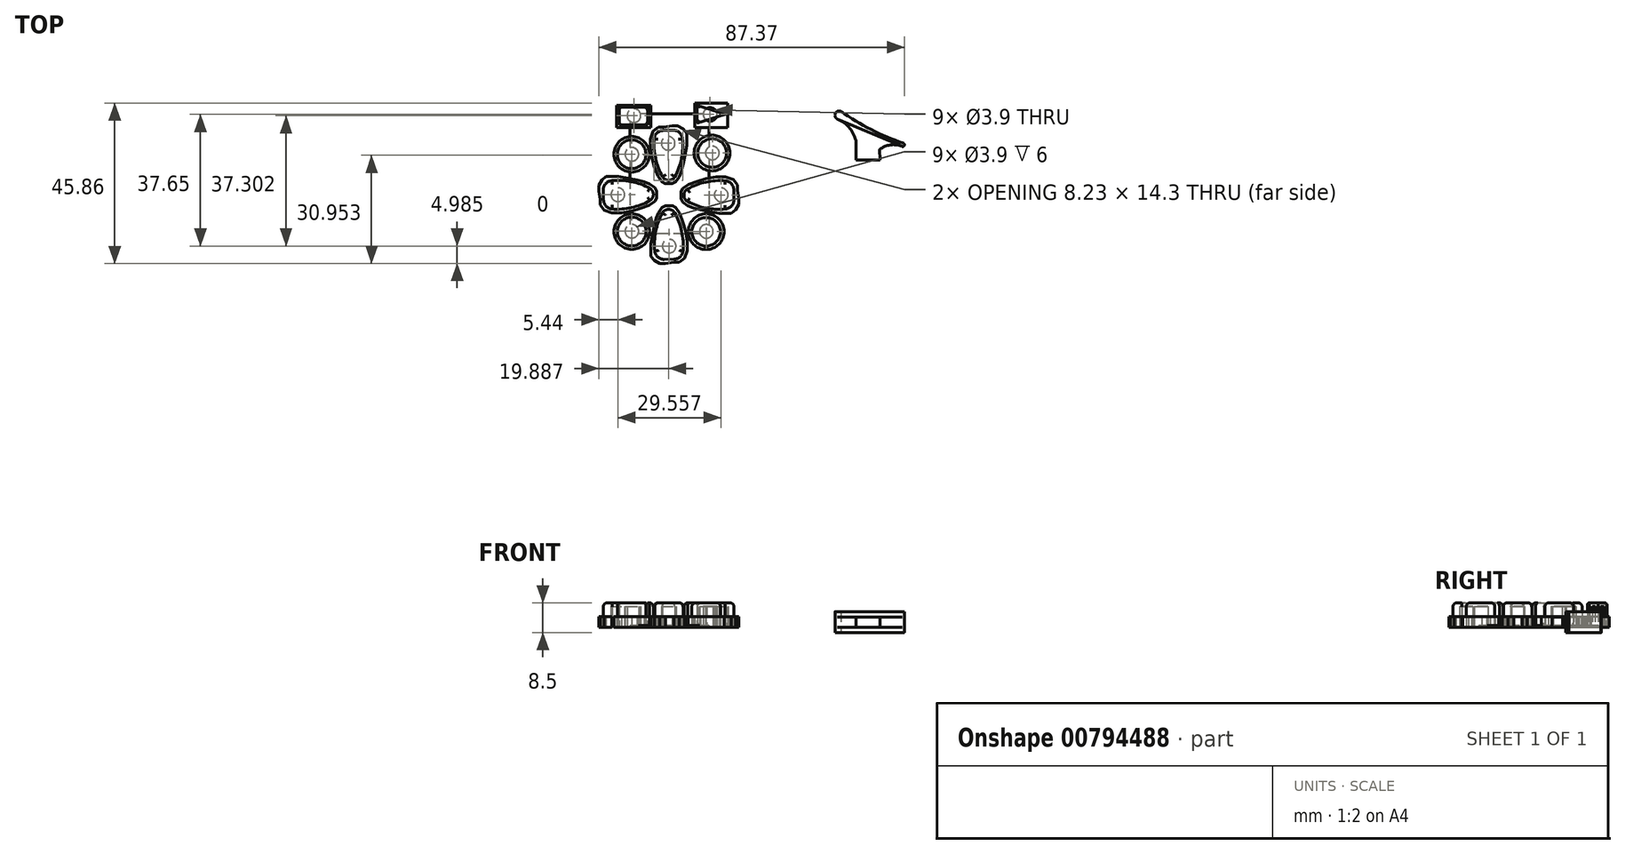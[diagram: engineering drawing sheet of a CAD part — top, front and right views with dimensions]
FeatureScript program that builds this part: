
annotation { "Feature Type Name" : "Feature", "Feature Type Description" : "" }
export const myFeature = defineFeature(function(context is Context, id is Id, definition is map)
    precondition{}
    {
        {
            var Q0;
            Q0=qCreatedBy(makeId("Top.planeOp"),FACE);
            var sketch = newSketch(context, id + "F0", { "sketchPlane" : qUnion([Q0])});
            skCircle(sketch, "E0", {"center": v(-35, -19.65) * mm, "radius": 4.1 * mm});
            skCircle(sketch, "E1", {"center": v(-58, -42.1) * mm, "radius": 4.1 * mm});
            skCircle(sketch, "E2", {"center": v(-58.02, -20.01) * mm, "radius": 4.1 * mm});
            skCircle(sketch, "E3", {"center": v(-36.71, -42.18) * mm, "radius": 4.1 * mm});
            skLineSegment(sketch, "E4", {"start": v(-39.3, -6.04) * mm, "end": v(-39.3, -11.07) * mm});
            skLineSegment(sketch, "E5", {"start": v(-39.3, -11.07) * mm, "end": v(-31.18, -8.6) * mm});
            skLineSegment(sketch, "E6", {"start": v(-31.18, -8.6) * mm, "end": v(-39.3, -6.04) * mm});
            skLineSegment(sketch, "E7", {"start": v(-61.5, -6.54) * mm, "end": v(-61.5, -11.57) * mm});
            skLineSegment(sketch, "E8", {"start": v(-61.5, -11.57) * mm, "end": v(-53.42, -11.57) * mm});
            skLineSegment(sketch, "E9", {"start": v(-53.42, -11.57) * mm, "end": v(-53.42, -6.54) * mm});
            skLineSegment(sketch, "E10", {"start": v(-53.42, -6.54) * mm, "end": v(-61.5, -6.54) * mm});
            skArc(sketch, "E11", {"start": v(-48.98, -13.2) * mm, "mid": v(-50.76, -13.92) * mm, "end": v(-51.58, -15.64) * mm});
            skLineSegment(sketch, "E12", {"start": v(-48.98, -13.2) * mm, "end": v(-46.14, -13.15) * mm});
            skArc(sketch, "E13", {"start": v(-43.48, -15.64) * mm, "mid": v(-44.3, -13.85) * mm, "end": v(-46.14, -13.15) * mm});
            skArc(sketch, "E14", {"start": v(-45.62, -26.42) * mm, "mid": v(-43.76, -21.19) * mm, "end": v(-43.48, -15.64) * mm});
            skArc(sketch, "E15", {"start": v(-51.58, -15.64) * mm, "mid": v(-51.17, -21.2) * mm, "end": v(-49.2, -26.42) * mm});
            skArc(sketch, "E16", {"start": v(-49.2, -26.42) * mm, "mid": v(-47.41, -27.45) * mm, "end": v(-45.62, -26.42) * mm});
            skArc(sketch, "E17", {"start": v(-66.07, -33.05) * mm, "mid": v(-65.35, -34.82) * mm, "end": v(-63.63, -35.65) * mm});
            skLineSegment(sketch, "E18", {"start": v(-66.07, -33.05) * mm, "end": v(-66.12, -30.2) * mm});
            skArc(sketch, "E19", {"start": v(-63.63, -27.55) * mm, "mid": v(-65.41, -28.37) * mm, "end": v(-66.12, -30.2) * mm});
            skArc(sketch, "E20", {"start": v(-52.85, -29.69) * mm, "mid": v(-58.08, -27.82) * mm, "end": v(-63.63, -27.55) * mm});
            skArc(sketch, "E21", {"start": v(-63.63, -35.65) * mm, "mid": v(-58.07, -35.24) * mm, "end": v(-52.85, -33.28) * mm});
            skArc(sketch, "E22", {"start": v(-52.85, -33.28) * mm, "mid": v(-51.82, -31.48) * mm, "end": v(-52.85, -29.69) * mm});
            skArc(sketch, "E23", {"start": v(-45.9, -50) * mm, "mid": v(-44.13, -49.29) * mm, "end": v(-43.3, -47.56) * mm});
            skLineSegment(sketch, "E24", {"start": v(-45.9, -50) * mm, "end": v(-48.75, -50.06) * mm});
            skArc(sketch, "E25", {"start": v(-51.4, -47.56) * mm, "mid": v(-50.58, -49.35) * mm, "end": v(-48.75, -50.06) * mm});
            skArc(sketch, "E26", {"start": v(-49.27, -36.78) * mm, "mid": v(-51.13, -42.02) * mm, "end": v(-51.4, -47.56) * mm});
            skArc(sketch, "E27", {"start": v(-43.3, -47.56) * mm, "mid": v(-43.71, -42) * mm, "end": v(-45.68, -36.78) * mm});
            skArc(sketch, "E28", {"start": v(-45.68, -36.78) * mm, "mid": v(-47.47, -35.76) * mm, "end": v(-49.27, -36.78) * mm});
            skArc(sketch, "E29", {"start": v(-28.82, -30.15) * mm, "mid": v(-29.54, -28.38) * mm, "end": v(-31.26, -27.55) * mm});
            skLineSegment(sketch, "E30", {"start": v(-28.82, -30.15) * mm, "end": v(-28.77, -33) * mm});
            skArc(sketch, "E31", {"start": v(-31.26, -35.66) * mm, "mid": v(-29.47, -34.83) * mm, "end": v(-28.77, -33) * mm});
            skArc(sketch, "E32", {"start": v(-42.04, -33.51) * mm, "mid": v(-36.8, -35.38) * mm, "end": v(-31.26, -35.66) * mm});
            skArc(sketch, "E33", {"start": v(-31.26, -27.55) * mm, "mid": v(-36.82, -27.96) * mm, "end": v(-42.04, -29.93) * mm});
            skArc(sketch, "E34", {"start": v(-42.04, -29.93) * mm, "mid": v(-43.07, -31.72) * mm, "end": v(-42.04, -33.51) * mm});
            skSolve(sketch);
        }
        {
            var Q0;
            Q0=makeQuery(id+"F0.imprint","IMPRINT",FACE,{"disambiguationData":[TD([[makeQuery(id+"F0.imprint","IMPRINT",EDGE,{"derivedFrom":sQuery(id+"F0.wireOp",EDGE,"E0")}),1.0]])]});
            var Q1;
            Q1=makeQuery(id+"F0.imprint","IMPRINT",FACE,{"disambiguationData":[TD([[makeQuery(id+"F0.imprint","IMPRINT",EDGE,{"derivedFrom":sQuery(id+"F0.wireOp",EDGE,"E1")}),1.0]])]});
            var Q2;
            Q2=makeQuery(id+"F0.imprint","IMPRINT",FACE,{"disambiguationData":[TD([[makeQuery(id+"F0.imprint","IMPRINT",EDGE,{"derivedFrom":sQuery(id+"F0.wireOp",EDGE,"E2")}),1.0]])]});
            var Q3;
            Q3=makeQuery(id+"F0.imprint","IMPRINT",FACE,{"disambiguationData":[TD([[makeQuery(id+"F0.imprint","IMPRINT",EDGE,{"derivedFrom":sQuery(id+"F0.wireOp",EDGE,"E3")}),1.0]])]});
            var Q4;
            Q4=makeQuery(id+"F0.imprint","IMPRINT",FACE,{"disambiguationData":[TD([[makeQuery(id+"F0.imprint","IMPRINT",EDGE,{"derivedFrom":sQuery(id+"F0.wireOp",EDGE,"E4")}),1.0]])]});
            var Q5;
            Q5=makeQuery(id+"F0.imprint","IMPRINT",FACE,{"disambiguationData":[TD([[makeQuery(id+"F0.imprint","IMPRINT",EDGE,{"derivedFrom":sQuery(id+"F0.wireOp",EDGE,"E7")}),1.0]])]});
            var Q6;
            Q6=makeQuery(id+"F0.imprint","IMPRINT",FACE,{"disambiguationData":[TD([[makeQuery(id+"F0.imprint","IMPRINT",EDGE,{"derivedFrom":sQuery(id+"F0.wireOp",EDGE,"E11")}),1.0]])]});
            var Q7;
            Q7=makeQuery(id+"F0.imprint","IMPRINT",FACE,{"disambiguationData":[TD([[makeQuery(id+"F0.imprint","IMPRINT",EDGE,{"derivedFrom":sQuery(id+"F0.wireOp",EDGE,"E17")}),1.0]])]});
            var Q8;
            Q8=makeQuery(id+"F0.imprint","IMPRINT",FACE,{"disambiguationData":[TD([[makeQuery(id+"F0.imprint","IMPRINT",EDGE,{"derivedFrom":sQuery(id+"F0.wireOp",EDGE,"E23")}),1.0]])]});
            var Q9;
            Q9=makeQuery(id+"F0.imprint","IMPRINT",FACE,{"disambiguationData":[TD([[makeQuery(id+"F0.imprint","IMPRINT",EDGE,{"derivedFrom":sQuery(id+"F0.wireOp",EDGE,"E29")}),1.0]])]});
            extrude(context, id + "F1", {"entities" : qUnion([Q0, Q1, Q2, Q3, Q4, Q5, Q6, Q7, Q8, Q9]), "depth" : 7 * mm, "offsetDistance" : 25 * mm});
        }
        {
            var Q0;
            Q0=makeQuery(id+"F1.opExtrude","CAP_FACE",FACE,{"disambiguationData":[OSD([sQuery(id+"F0.wireOp",EDGE,"E11"),sQuery(id+"F0.wireOp",EDGE,"E12"),sQuery(id+"F0.wireOp",EDGE,"E13"),sQuery(id+"F0.wireOp",EDGE,"E14"),sQuery(id+"F0.wireOp",EDGE,"E15"),sQuery(id+"F0.wireOp",EDGE,"E16")])],"isStart":false});
            var Q1;
            Q1=makeQuery(id+"F1.opExtrude","CAP_FACE",FACE,{"disambiguationData":[OSD([sQuery(id+"F0.wireOp",EDGE,"E2")])],"isStart":false});
            var Q2;
            Q2=makeQuery(id+"F1.opExtrude","CAP_FACE",FACE,{"disambiguationData":[OSD([sQuery(id+"F0.wireOp",EDGE,"E17"),sQuery(id+"F0.wireOp",EDGE,"E18"),sQuery(id+"F0.wireOp",EDGE,"E19"),sQuery(id+"F0.wireOp",EDGE,"E20"),sQuery(id+"F0.wireOp",EDGE,"E21"),sQuery(id+"F0.wireOp",EDGE,"E22")])],"isStart":false});
            var Q3;
            Q3=makeQuery(id+"F1.opExtrude","CAP_FACE",FACE,{"disambiguationData":[OSD([sQuery(id+"F0.wireOp",EDGE,"E0")])],"isStart":false});
            var Q4;
            Q4=makeQuery(id+"F1.opExtrude","CAP_FACE",FACE,{"disambiguationData":[OSD([sQuery(id+"F0.wireOp",EDGE,"E29"),sQuery(id+"F0.wireOp",EDGE,"E30"),sQuery(id+"F0.wireOp",EDGE,"E31"),sQuery(id+"F0.wireOp",EDGE,"E32"),sQuery(id+"F0.wireOp",EDGE,"E33"),sQuery(id+"F0.wireOp",EDGE,"E34")])],"isStart":false});
            var Q5;
            Q5=makeQuery(id+"F1.opExtrude","CAP_FACE",FACE,{"disambiguationData":[OSD([sQuery(id+"F0.wireOp",EDGE,"E3")])],"isStart":false});
            var Q6;
            Q6=makeQuery(id+"F1.opExtrude","CAP_FACE",FACE,{"disambiguationData":[OSD([sQuery(id+"F0.wireOp",EDGE,"E23"),sQuery(id+"F0.wireOp",EDGE,"E24"),sQuery(id+"F0.wireOp",EDGE,"E25"),sQuery(id+"F0.wireOp",EDGE,"E26"),sQuery(id+"F0.wireOp",EDGE,"E27"),sQuery(id+"F0.wireOp",EDGE,"E28")])],"isStart":false});
            fillet(context, id + "F2", {"entities" : qUnion([Q0, Q1, Q2, Q3, Q4, Q5, Q6]), "radius" : 1.12 * mm, "tangentPropagation" : true, "allowEdgeOverflow" : false});
        }
        {
            var Q0;
            Q0=makeQuery(id+"F1.opExtrude","CAP_FACE",FACE,{"disambiguationData":[OSD([sQuery(id+"F0.wireOp",EDGE,"E7"),sQuery(id+"F0.wireOp",EDGE,"E8"),sQuery(id+"F0.wireOp",EDGE,"E9"),sQuery(id+"F0.wireOp",EDGE,"E10")])],"isStart":false});
            var Q1;
            Q1=makeQuery(id+"F1.opExtrude","CAP_FACE",FACE,{"disambiguationData":[OSD([sQuery(id+"F0.wireOp",EDGE,"E4"),sQuery(id+"F0.wireOp",EDGE,"E5"),sQuery(id+"F0.wireOp",EDGE,"E6")])],"isStart":false});
            fillet(context, id + "F3", {"entities" : qUnion([Q0, Q1]), "radius" : .5 * mm, "tangentPropagation" : true, "allowEdgeOverflow" : false});
        }
        {
            var Q0;
            Q0=makeQuery(id+"F1.opExtrude","CAP_FACE",FACE,{"disambiguationData":[OSD([sQuery(id+"F0.wireOp",EDGE,"E11"),sQuery(id+"F0.wireOp",EDGE,"E12"),sQuery(id+"F0.wireOp",EDGE,"E13"),sQuery(id+"F0.wireOp",EDGE,"E14"),sQuery(id+"F0.wireOp",EDGE,"E15"),sQuery(id+"F0.wireOp",EDGE,"E16")])],"isStart":true});
            var sketch = newSketch(context, id + "F4", { "sketchPlane" : qUnion([Q0])});
            skCircle(sketch, "E35", {"center": v(-57.95, 20.02) * mm, "radius": 1.95 * mm});
            skCircle(sketch, "E36", {"center": v(-34.94, 19.66) * mm, "radius": 1.95 * mm});
            skCircle(sketch, "E37", {"center": v(-36.66, 42.04) * mm, "radius": 1.95 * mm});
            skCircle(sketch, "E38", {"center": v(-57.95, 42.01) * mm, "radius": 1.95 * mm});
            skCircle(sketch, "E39", {"center": v(-32.4, 31.62) * mm, "radius": 1.95 * mm});
            skCircle(sketch, "E40", {"center": v(-61.96, 31.55) * mm, "radius": 1.95 * mm});
            skCircle(sketch, "E41", {"center": v(-47.28, 46.26) * mm, "radius": 1.95 * mm});
            skCircle(sketch, "E42", {"center": v(-47.56, 16.87) * mm, "radius": 1.95 * mm});
            skPoint(sketch, "E43", {"position": v(-47.56, 13.17) * mm});
            skCircle(sketch, "E44", {"center": v(-57.36, 8.96) * mm, "radius": 1.95 * mm});
            skCircle(sketch, "E45", {"center": v(-35.59, 8.61) * mm, "radius": 1.95 * mm});
            skSolve(sketch);
        }
        {
            var Q0;
            Q0=makeQuery(id+"F4.imprint","IMPRINT",FACE,{"disambiguationData":[TD([[makeQuery(id+"F4.imprint","IMPRINT",EDGE,{"derivedFrom":sQuery(id+"F4.wireOp",EDGE,"E42")}),-1.0]])]});
            var sketch = newSketch(context, id + "F5", { "sketchPlane" : qUnion([Q0])});
            skCircle(sketch, "E46", {"center": v(-35.06, 19.67) * mm, "radius": 5.1 * mm});
            skCircle(sketch, "E47", {"center": v(-58, 20) * mm, "radius": 5.1 * mm});
            skCircle(sketch, "E48", {"center": v(-57.97, 42.11) * mm, "radius": 5.1 * mm});
            skCircle(sketch, "E49", {"center": v(-36.7, 42.13) * mm, "radius": 5.1 * mm});
            skLineSegment(sketch, "E50", {"start": v(-27.77, 30.26) * mm, "end": v(-27.77, 28.82) * mm});
            skLineSegment(sketch, "E51", {"start": v(-27.77, 28.82) * mm, "end": v(-28.94, 27.23) * mm});
            skLineSegment(sketch, "E52", {"start": v(-28.94, 27.23) * mm, "end": v(-31.14, 26.48) * mm});
            skLineSegment(sketch, "E53", {"start": v(-31.14, 26.48) * mm, "end": v(-33.85, 26.48) * mm});
            skLineSegment(sketch, "E54", {"start": v(-33.85, 26.48) * mm, "end": v(-36.84, 27) * mm});
            skLineSegment(sketch, "E55", {"start": v(-36.84, 27) * mm, "end": v(-39.18, 27.7) * mm});
            skLineSegment(sketch, "E56", {"start": v(-39.18, 27.7) * mm, "end": v(-41.75, 28.67) * mm});
            skLineSegment(sketch, "E57", {"start": v(-41.75, 28.67) * mm, "end": v(-43.4, 29.8) * mm});
            skLineSegment(sketch, "E58", {"start": v(-43.4, 29.8) * mm, "end": v(-43.95, 30.69) * mm});
            skLineSegment(sketch, "E59", {"start": v(-43.95, 30.69) * mm, "end": v(-43.95, 31.71) * mm});
            skLineSegment(sketch, "E60", {"start": v(-43.95, 31.71) * mm, "end": v(-43.95, 32.7) * mm});
            skLineSegment(sketch, "E61", {"start": v(-43.95, 32.7) * mm, "end": v(-43.4, 33.68) * mm});
            skLineSegment(sketch, "E62", {"start": v(-43.4, 33.68) * mm, "end": v(-41.94, 34.7) * mm});
            skLineSegment(sketch, "E63", {"start": v(-41.94, 34.7) * mm, "end": v(-40.35, 35.36) * mm});
            skLineSegment(sketch, "E64", {"start": v(-40.35, 35.36) * mm, "end": v(-38.3, 35.92) * mm});
            skLineSegment(sketch, "E65", {"start": v(-38.3, 35.92) * mm, "end": v(-35.72, 36.4) * mm});
            skLineSegment(sketch, "E66", {"start": v(-35.72, 36.4) * mm, "end": v(-33, 36.86) * mm});
            skLineSegment(sketch, "E67", {"start": v(-33, 36.86) * mm, "end": v(-31.1, 36.86) * mm});
            skLineSegment(sketch, "E68", {"start": v(-31.1, 36.86) * mm, "end": v(-29.5, 36.86) * mm});
            skLineSegment(sketch, "E69", {"start": v(-29.5, 36.86) * mm, "end": v(-28.24, 35.92) * mm});
            skLineSegment(sketch, "E70", {"start": v(-28.24, 35.92) * mm, "end": v(-27.4, 34.29) * mm});
            skLineSegment(sketch, "E71", {"start": v(-27.4, 34.29) * mm, "end": v(-27.4, 32.7) * mm});
            skLineSegment(sketch, "E72", {"start": v(-27.4, 32.7) * mm, "end": v(-27.77, 30.26) * mm});
            skLineSegment(sketch, "E73", {"start": v(-67.03, 32.97) * mm, "end": v(-67.03, 34.42) * mm});
            skLineSegment(sketch, "E74", {"start": v(-67.03, 34.42) * mm, "end": v(-65.86, 36) * mm});
            skLineSegment(sketch, "E75", {"start": v(-65.86, 36) * mm, "end": v(-63.66, 36.76) * mm});
            skLineSegment(sketch, "E76", {"start": v(-63.66, 36.76) * mm, "end": v(-60.95, 36.76) * mm});
            skLineSegment(sketch, "E77", {"start": v(-60.95, 36.76) * mm, "end": v(-57.96, 36.24) * mm});
            skLineSegment(sketch, "E78", {"start": v(-57.96, 36.24) * mm, "end": v(-55.62, 35.54) * mm});
            skLineSegment(sketch, "E79", {"start": v(-55.62, 35.54) * mm, "end": v(-53.05, 34.56) * mm});
            skLineSegment(sketch, "E80", {"start": v(-53.05, 34.56) * mm, "end": v(-51.41, 33.44) * mm});
            skLineSegment(sketch, "E81", {"start": v(-51.41, 33.44) * mm, "end": v(-50.85, 32.55) * mm});
            skLineSegment(sketch, "E82", {"start": v(-50.85, 32.55) * mm, "end": v(-50.85, 31.52) * mm});
            skLineSegment(sketch, "E83", {"start": v(-50.85, 31.52) * mm, "end": v(-50.85, 30.54) * mm});
            skLineSegment(sketch, "E84", {"start": v(-50.85, 30.54) * mm, "end": v(-51.41, 29.56) * mm});
            skLineSegment(sketch, "E85", {"start": v(-51.41, 29.56) * mm, "end": v(-52.86, 28.53) * mm});
            skLineSegment(sketch, "E86", {"start": v(-52.86, 28.53) * mm, "end": v(-54.45, 27.87) * mm});
            skLineSegment(sketch, "E87", {"start": v(-54.45, 27.87) * mm, "end": v(-56.5, 27.31) * mm});
            skLineSegment(sketch, "E88", {"start": v(-56.5, 27.31) * mm, "end": v(-59.08, 26.84) * mm});
            skLineSegment(sketch, "E89", {"start": v(-59.08, 26.84) * mm, "end": v(-61.8, 26.38) * mm});
            skLineSegment(sketch, "E90", {"start": v(-61.8, 26.38) * mm, "end": v(-63.7, 26.38) * mm});
            skLineSegment(sketch, "E91", {"start": v(-63.7, 26.38) * mm, "end": v(-65.3, 26.38) * mm});
            skLineSegment(sketch, "E92", {"start": v(-65.3, 26.38) * mm, "end": v(-66.56, 27.31) * mm});
            skLineSegment(sketch, "E93", {"start": v(-66.56, 27.31) * mm, "end": v(-67.4, 28.95) * mm});
            skLineSegment(sketch, "E94", {"start": v(-67.4, 28.95) * mm, "end": v(-67.4, 30.54) * mm});
            skLineSegment(sketch, "E95", {"start": v(-67.4, 30.54) * mm, "end": v(-67.03, 32.97) * mm});
            skLineSegment(sketch, "E96", {"start": v(-45.9, 50.88) * mm, "end": v(-44.46, 50.88) * mm});
            skLineSegment(sketch, "E97", {"start": v(-44.46, 50.88) * mm, "end": v(-42.87, 49.7) * mm});
            skLineSegment(sketch, "E98", {"start": v(-42.87, 49.7) * mm, "end": v(-42.12, 47.5) * mm});
            skLineSegment(sketch, "E99", {"start": v(-42.12, 47.5) * mm, "end": v(-42.12, 44.8) * mm});
            skLineSegment(sketch, "E100", {"start": v(-42.12, 44.8) * mm, "end": v(-42.63, 41.8) * mm});
            skLineSegment(sketch, "E101", {"start": v(-42.63, 41.8) * mm, "end": v(-43.33, 39.47) * mm});
            skLineSegment(sketch, "E102", {"start": v(-43.33, 39.47) * mm, "end": v(-44.32, 36.9) * mm});
            skLineSegment(sketch, "E103", {"start": v(-44.32, 36.9) * mm, "end": v(-45.44, 35.26) * mm});
            skLineSegment(sketch, "E104", {"start": v(-45.44, 35.26) * mm, "end": v(-46.33, 34.7) * mm});
            skLineSegment(sketch, "E105", {"start": v(-46.33, 34.7) * mm, "end": v(-47.36, 34.7) * mm});
            skLineSegment(sketch, "E106", {"start": v(-47.36, 34.7) * mm, "end": v(-48.34, 34.7) * mm});
            skLineSegment(sketch, "E107", {"start": v(-48.34, 34.7) * mm, "end": v(-49.32, 35.26) * mm});
            skLineSegment(sketch, "E108", {"start": v(-49.32, 35.26) * mm, "end": v(-50.35, 36.7) * mm});
            skLineSegment(sketch, "E109", {"start": v(-50.35, 36.7) * mm, "end": v(-51, 38.3) * mm});
            skLineSegment(sketch, "E110", {"start": v(-51, 38.3) * mm, "end": v(-51.56, 40.35) * mm});
            skLineSegment(sketch, "E111", {"start": v(-51.56, 40.35) * mm, "end": v(-52.03, 42.93) * mm});
            skLineSegment(sketch, "E112", {"start": v(-52.03, 42.93) * mm, "end": v(-52.5, 45.64) * mm});
            skLineSegment(sketch, "E113", {"start": v(-52.5, 45.64) * mm, "end": v(-52.5, 47.56) * mm});
            skLineSegment(sketch, "E114", {"start": v(-52.5, 47.56) * mm, "end": v(-52.5, 49.15) * mm});
            skLineSegment(sketch, "E115", {"start": v(-52.5, 49.15) * mm, "end": v(-51.56, 50.4) * mm});
            skLineSegment(sketch, "E116", {"start": v(-51.56, 50.4) * mm, "end": v(-49.93, 51.25) * mm});
            skLineSegment(sketch, "E117", {"start": v(-49.93, 51.25) * mm, "end": v(-48.34, 51.25) * mm});
            skLineSegment(sketch, "E118", {"start": v(-48.34, 51.25) * mm, "end": v(-45.9, 50.88) * mm});
            skLineSegment(sketch, "E119", {"start": v(-48.89, 12.25) * mm, "end": v(-50.34, 12.25) * mm});
            skLineSegment(sketch, "E120", {"start": v(-50.34, 12.25) * mm, "end": v(-51.93, 13.42) * mm});
            skLineSegment(sketch, "E121", {"start": v(-51.93, 13.42) * mm, "end": v(-52.68, 15.62) * mm});
            skLineSegment(sketch, "E122", {"start": v(-52.68, 15.62) * mm, "end": v(-52.68, 18.33) * mm});
            skLineSegment(sketch, "E123", {"start": v(-52.68, 18.33) * mm, "end": v(-52.16, 21.33) * mm});
            skLineSegment(sketch, "E124", {"start": v(-52.16, 21.33) * mm, "end": v(-51.46, 23.66) * mm});
            skLineSegment(sketch, "E125", {"start": v(-51.46, 23.66) * mm, "end": v(-50.48, 26.24) * mm});
            skLineSegment(sketch, "E126", {"start": v(-50.48, 26.24) * mm, "end": v(-49.36, 27.87) * mm});
            skLineSegment(sketch, "E127", {"start": v(-49.36, 27.87) * mm, "end": v(-48.47, 28.43) * mm});
            skLineSegment(sketch, "E128", {"start": v(-48.47, 28.43) * mm, "end": v(-47.44, 28.43) * mm});
            skLineSegment(sketch, "E129", {"start": v(-47.44, 28.43) * mm, "end": v(-46.46, 28.43) * mm});
            skLineSegment(sketch, "E130", {"start": v(-46.46, 28.43) * mm, "end": v(-45.47, 27.87) * mm});
            skLineSegment(sketch, "E131", {"start": v(-45.47, 27.87) * mm, "end": v(-44.45, 26.42) * mm});
            skLineSegment(sketch, "E132", {"start": v(-44.45, 26.42) * mm, "end": v(-43.8, 24.83) * mm});
            skLineSegment(sketch, "E133", {"start": v(-43.8, 24.83) * mm, "end": v(-43.23, 22.77) * mm});
            skLineSegment(sketch, "E134", {"start": v(-43.23, 22.77) * mm, "end": v(-42.76, 20.2) * mm});
            skLineSegment(sketch, "E135", {"start": v(-42.76, 20.2) * mm, "end": v(-42.3, 17.5) * mm});
            skLineSegment(sketch, "E136", {"start": v(-42.3, 17.5) * mm, "end": v(-42.3, 15.57) * mm});
            skLineSegment(sketch, "E137", {"start": v(-42.3, 15.57) * mm, "end": v(-42.3, 13.98) * mm});
            skLineSegment(sketch, "E138", {"start": v(-42.3, 13.98) * mm, "end": v(-43.23, 12.72) * mm});
            skLineSegment(sketch, "E139", {"start": v(-43.23, 12.72) * mm, "end": v(-44.87, 11.88) * mm});
            skLineSegment(sketch, "E140", {"start": v(-44.87, 11.88) * mm, "end": v(-46.46, 11.88) * mm});
            skLineSegment(sketch, "E141", {"start": v(-46.46, 11.88) * mm, "end": v(-48.89, 12.25) * mm});
            skLineSegment(sketch, "E142.bottom", {"start": v(-52.57, 6) * mm, "end": v(-62.27, 6) * mm});
            skLineSegment(sketch, "E142.top", {"start": v(-52.57, 12.35) * mm, "end": v(-62.27, 12.35) * mm});
            skLineSegment(sketch, "E142.left", {"start": v(-52.57, 6) * mm, "end": v(-52.57, 12.35) * mm});
            skLineSegment(sketch, "E142.right", {"start": v(-62.27, 6) * mm, "end": v(-62.27, 12.35) * mm});
            skLineSegment(sketch, "E143.bottom", {"start": v(-39.95, 5.39) * mm, "end": v(-30.54, 5.39) * mm});
            skLineSegment(sketch, "E143.top", {"start": v(-39.95, 12.31) * mm, "end": v(-30.54, 12.31) * mm});
            skLineSegment(sketch, "E143.left", {"start": v(-39.95, 5.39) * mm, "end": v(-39.95, 12.31) * mm});
            skLineSegment(sketch, "E143.right", {"start": v(-30.54, 5.39) * mm, "end": v(-30.54, 12.31) * mm});
            skSolve(sketch);
        }
        {
            var Q0;
            Q0=makeQuery(id+"F5.imprint","IMPRINT",FACE,{"disambiguationData":[TD([[makeQuery(id+"F5.imprint","IMPRINT",EDGE,{"derivedFrom":sQuery(id+"F5.wireOp",EDGE,"E143.bottom")}),1.0]])]});
            var Q1;
            Q1=makeQuery(id+"F5.imprint","IMPRINT",FACE,{"disambiguationData":[TD([[makeQuery(id+"F5.imprint","IMPRINT",EDGE,{"derivedFrom":sQuery(id+"F5.wireOp",EDGE,"E142.bottom")}),-1.0]])]});
            var Q2;
            Q2=makeQuery(id+"F5.imprint","IMPRINT",FACE,{"disambiguationData":[TD([[makeQuery(id+"F5.imprint","IMPRINT",EDGE,{"derivedFrom":sQuery(id+"F5.wireOp",EDGE,"E119")}),-1.0]])]});
            var Q3;
            Q3=makeQuery(id+"F5.imprint","IMPRINT",FACE,{"disambiguationData":[TD([[makeQuery(id+"F5.imprint","IMPRINT",EDGE,{"derivedFrom":sQuery(id+"F5.wireOp",EDGE,"E46")}),1.0]])]});
            var Q4;
            Q4=makeQuery(id+"F5.imprint","IMPRINT",FACE,{"disambiguationData":[TD([[makeQuery(id+"F5.imprint","IMPRINT",EDGE,{"derivedFrom":sQuery(id+"F5.wireOp",EDGE,"E47")}),1.0]])]});
            var Q5;
            Q5=makeQuery(id+"F5.imprint","IMPRINT",FACE,{"disambiguationData":[TD([[makeQuery(id+"F5.imprint","IMPRINT",EDGE,{"derivedFrom":sQuery(id+"F5.wireOp",EDGE,"E73")}),-1.0]])]});
            var Q6;
            Q6=makeQuery(id+"F5.imprint","IMPRINT",FACE,{"disambiguationData":[TD([[makeQuery(id+"F5.imprint","IMPRINT",EDGE,{"derivedFrom":sQuery(id+"F5.wireOp",EDGE,"E50")}),-1.0]])]});
            var Q7;
            Q7=makeQuery(id+"F5.imprint","IMPRINT",FACE,{"disambiguationData":[TD([[makeQuery(id+"F5.imprint","IMPRINT",EDGE,{"derivedFrom":sQuery(id+"F5.wireOp",EDGE,"E96")}),-1.0]])]});
            var Q8;
            Q8=makeQuery(id+"F5.imprint","IMPRINT",FACE,{"disambiguationData":[TD([[makeQuery(id+"F5.imprint","IMPRINT",EDGE,{"derivedFrom":sQuery(id+"F5.wireOp",EDGE,"E48")}),1.0]])]});
            var Q9;
            Q9=makeQuery(id+"F5.imprint","IMPRINT",FACE,{"disambiguationData":[TD([[makeQuery(id+"F5.imprint","IMPRINT",EDGE,{"derivedFrom":sQuery(id+"F5.wireOp",EDGE,"E49")}),1.0]])]});
            extrude(context, id + "F6", {"entities" : qUnion([Q0, Q1, Q2, Q3, Q4, Q5, Q6, Q7, Q8, Q9]), "oppositeDirection" : true, "depth" : 3 * mm, "offsetDistance" : 25 * mm});
        }
        {
            var Q0;
            Q0=makeQuery(id+"F1.opExtrude","CAP_FACE",FACE,{"disambiguationData":[OSD([sQuery(id+"F0.wireOp",EDGE,"E11"),sQuery(id+"F0.wireOp",EDGE,"E12"),sQuery(id+"F0.wireOp",EDGE,"E13"),sQuery(id+"F0.wireOp",EDGE,"E14"),sQuery(id+"F0.wireOp",EDGE,"E15"),sQuery(id+"F0.wireOp",EDGE,"E16")])],"isStart":true});
            var sketch = newSketch(context, id + "F7", { "sketchPlane" : qUnion([Q0])});
            skLineSegment(sketch, "E144.bottom", {"start": v(-35.85, 8.43) * mm, "end": v(-58.52, 8.43) * mm});
            skLineSegment(sketch, "E144.top", {"start": v(-35.85, 42.69) * mm, "end": v(-58.52, 42.69) * mm});
            skLineSegment(sketch, "E144.left", {"start": v(-35.85, 8.43) * mm, "end": v(-35.85, 42.69) * mm});
            skLineSegment(sketch, "E144.right", {"start": v(-58.52, 8.43) * mm, "end": v(-58.52, 42.69) * mm});
            skSolve(sketch);
        }
        {
            var Q0;
            Q0=makeQuery(id+"F7.imprint","IMPRINT",FACE,{"disambiguationData":[TD([[makeQuery(id+"F7.imprint","IMPRINT",EDGE,{"derivedFrom":sQuery(id+"F7.wireOp",EDGE,"E144.bottom")}),-1.0]])]});
            extrude(context, id + "F8", {"entities" : qUnion([Q0]), "oppositeDirection" : true, "depth" : .5 * mm, "offsetDistance" : 25 * mm});
        }
        {
            var Q0;
            Q0=makeQuery(id+"F4.imprint","IMPRINT",FACE,{"disambiguationData":[TD([[makeQuery(id+"F4.imprint","IMPRINT",EDGE,{"derivedFrom":sQuery(id+"F4.wireOp",EDGE,"E45")}),1.0]])]});
            var Q1;
            Q1=makeQuery(id+"F4.imprint","IMPRINT",FACE,{"disambiguationData":[TD([[makeQuery(id+"F4.imprint","IMPRINT",EDGE,{"derivedFrom":sQuery(id+"F4.wireOp",EDGE,"E36")}),1.0]])]});
            var Q2;
            Q2=makeQuery(id+"F4.imprint","IMPRINT",FACE,{"disambiguationData":[TD([[makeQuery(id+"F4.imprint","IMPRINT",EDGE,{"derivedFrom":sQuery(id+"F4.wireOp",EDGE,"E39")}),1.0]])]});
            var Q3;
            Q3=makeQuery(id+"F4.imprint","IMPRINT",FACE,{"disambiguationData":[TD([[makeQuery(id+"F4.imprint","IMPRINT",EDGE,{"derivedFrom":sQuery(id+"F4.wireOp",EDGE,"E37")}),1.0]])]});
            var Q4;
            Q4=makeQuery(id+"F4.imprint","IMPRINT",FACE,{"disambiguationData":[TD([[makeQuery(id+"F4.imprint","IMPRINT",EDGE,{"derivedFrom":sQuery(id+"F4.wireOp",EDGE,"E41")}),1.0]])]});
            var Q5;
            Q5=makeQuery(id+"F4.imprint","IMPRINT",FACE,{"disambiguationData":[TD([[makeQuery(id+"F4.imprint","IMPRINT",EDGE,{"derivedFrom":sQuery(id+"F4.wireOp",EDGE,"E38")}),1.0]])]});
            var Q6;
            Q6=makeQuery(id+"F4.imprint","IMPRINT",FACE,{"disambiguationData":[TD([[makeQuery(id+"F4.imprint","IMPRINT",EDGE,{"derivedFrom":sQuery(id+"F4.wireOp",EDGE,"E40")}),1.0]])]});
            var Q7;
            Q7=makeQuery(id+"F4.imprint","IMPRINT",FACE,{"disambiguationData":[TD([[makeQuery(id+"F4.imprint","IMPRINT",EDGE,{"derivedFrom":sQuery(id+"F4.wireOp",EDGE,"E35")}),1.0]])]});
            var Q8;
            Q8=makeQuery(id+"F4.imprint","IMPRINT",FACE,{"disambiguationData":[TD([[makeQuery(id+"F4.imprint","IMPRINT",EDGE,{"derivedFrom":sQuery(id+"F4.wireOp",EDGE,"E44")}),1.0]])]});
            var Q9;
            Q9=makeQuery(id+"F4.imprint","IMPRINT",FACE,{"disambiguationData":[TD([[makeQuery(id+"F4.imprint","IMPRINT",EDGE,{"derivedFrom":sQuery(id+"F4.wireOp",EDGE,"E42")}),1.0]])]});
            var Q10;
            Q10=sQuery(id+"F4.wireOp",EDGE,"E45");
            var Q11;
            Q11=sQuery(id+"F4.wireOp",EDGE,"E44");
            var Q12;
            Q12=sQuery(id+"F4.wireOp",EDGE,"E36");
            var Q13;
            Q13=sQuery(id+"F4.wireOp",EDGE,"E42");
            var Q14;
            Q14=sQuery(id+"F4.wireOp",EDGE,"E35");
            var Q15;
            Q15=sQuery(id+"F4.wireOp",EDGE,"E37");
            var Q16;
            Q16=sQuery(id+"F4.wireOp",EDGE,"E39");
            var Q17;
            Q17=sQuery(id+"F4.wireOp",EDGE,"E40");
            var Q18;
            Q18=sQuery(id+"F4.wireOp",EDGE,"E38");
            var Q19;
            Q19=sQuery(id+"F4.wireOp",EDGE,"E41");
            extrude(context, id + "F9", {"entities" : qUnion([Q0, Q1, Q2, Q3, Q4, Q5, Q6, Q7, Q8, Q9]), "operationType" : NewBodyOperationType.REMOVE, "surfaceEntities" : qUnion([Q10, Q11, Q12, Q13, Q14, Q15, Q16, Q17, Q18, Q19]), "endBound" : BoundingType.SYMMETRIC, "oppositeDirection" : true, "depth" : 12 * mm, "offsetDistance" : 25 * mm});
        }
        {
            var Q0;
            Q0=qCreatedBy(makeId("Top.planeOp"),FACE);
            var sketch = newSketch(context, id + "F10", { "sketchPlane" : qUnion([Q0])});
            skArc(sketch, "E145", {"start": v(1.78, -7.73) * mm, "mid": v(10.42, -12.9) * mm, "end": v(19.67, -16.87) * mm});
            skArc(sketch, "E146", {"start": v(1.78, -7.73) * mm, "mid": v(0.2, -8.37) * mm, "end": v(0.84, -9.93) * mm});
            skArc(sketch, "E147", {"start": v(19.3, -17.77) * mm, "mid": v(19.93, -17.5) * mm, "end": v(19.67, -16.87) * mm});
            skLineSegment(sketch, "E148.0", {"start": v(19.3, -17.77) * mm, "end": v(19.67, -16.87) * mm, "construction": true});
            skLineSegment(sketch, "E149.0", {"start": v(0.84, -9.93) * mm, "end": v(1.78, -7.73) * mm, "construction": true});
            skArc(sketch, "E150", {"start": v(6.2, -16.64) * mm, "mid": v(4.37, -12.6) * mm, "end": v(0.84, -9.93) * mm});
            skArc(sketch, "E151", {"start": v(19.3, -17.77) * mm, "mid": v(15.96, -17.32) * mm, "end": v(12.87, -18.65) * mm});
            skLineSegment(sketch, "E152", {"start": v(6.2, -16.64) * mm, "end": v(6.2, -21.69) * mm});
            skLineSegment(sketch, "E153", {"start": v(6.2, -21.69) * mm, "end": v(13.01, -21.69) * mm});
            skLineSegment(sketch, "E154", {"start": v(13.01, -21.69) * mm, "end": v(12.87, -18.65) * mm});
            skLineSegment(sketch, "E155", {"start": v(0.84, -9.93) * mm, "end": v(19.3, -17.77) * mm});
            skSolve(sketch);
        }
        {
            var Q0;
            Q0=makeQuery(id+"F10.imprint","IMPRINT",FACE,{"disambiguationData":[TD([[makeQuery(id+"F10.imprint","IMPRINT",EDGE,{"derivedFrom":sQuery(id+"F10.wireOp",EDGE,"E150")}),-1.0]])]});
            extrude(context, id + "F11", {"entities" : qUnion([Q0]), "depth" : 2.88 * mm, "offsetDistance" : 25 * mm});
        }
        {
            var Q0;
            Q0=makeQuery(id+"F10.imprint","IMPRINT",FACE,{"disambiguationData":[TD([[makeQuery(id+"F10.imprint","IMPRINT",EDGE,{"derivedFrom":sQuery(id+"F10.wireOp",EDGE,"E145")}),-1.0]])]});
            extrude(context, id + "F12", {"entities" : qUnion([Q0]), "operationType" : NewBodyOperationType.ADD, "depth" : 4.5 * mm, "offsetDistance" : 25 * mm, "hasSecondDirection" : true, "secondDirectionOppositeDirection" : true, "secondDirectionDepth" : 1.5 * mm});
        }
    });
